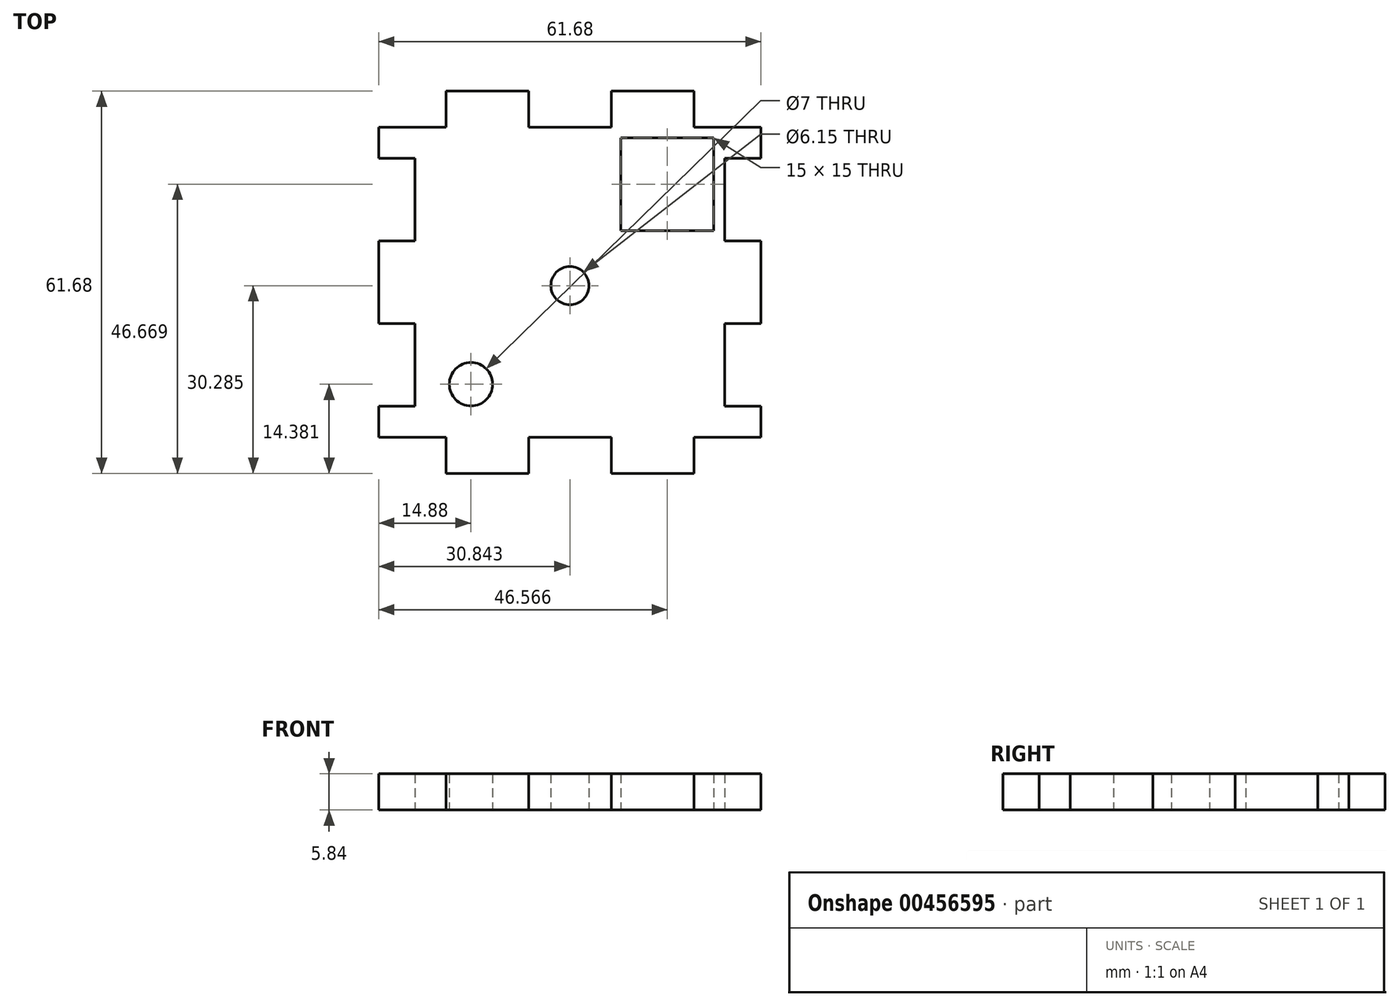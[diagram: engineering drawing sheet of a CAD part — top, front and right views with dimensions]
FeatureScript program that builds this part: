
annotation { "Feature Type Name" : "Feature", "Feature Type Description" : "" }
export const myFeature = defineFeature(function(context is Context, id is Id, definition is map)
    precondition{}
    {
        {
            var Q0;
            Q0=qCreatedBy(makeId("Top.planeOp"),FACE);
            var sketch = newSketch(context, id + "F0", { "sketchPlane" : qUnion([Q0])});
            skLineSegment(sketch, "E0.bottom", {"start": v(-25, 25.5) * mm, "end": v(-20, 25.5) * mm});
            skLineSegment(sketch, "E0.top", {"start": v(-25, -24.5) * mm, "end": v(-20, -24.5) * mm});
            skLineSegment(sketch, "E0.left", {"start": v(-25, 20.5) * mm, "end": v(-25, 7.17) * mm});
            skLineSegment(sketch, "E0.right", {"start": v(25, 20.5) * mm, "end": v(25, 7.17) * mm});
            skLineSegment(sketch, "E1.bottom", {"start": v(-20, 31.35) * mm, "end": v(-6.67, 31.35) * mm});
            skLineSegment(sketch, "E1.top", {"start": v(-20, -30.33) * mm, "end": v(-6.67, -30.33) * mm});
            skLineSegment(sketch, "E1.left", {"start": v(-30.84, 25.5) * mm, "end": v(-30.84, 20.5) * mm});
            skLineSegment(sketch, "E1.right", {"start": v(30.84, 25.5) * mm, "end": v(30.84, 20.5) * mm});
            skCircle(sketch, "E2", {"center": v(-15.96, -15.95) * mm, "radius": 3.5 * mm});
            skLineSegment(sketch, "E3.bottom", {"start": v(8.23, 23.84) * mm, "end": v(23.23, 23.84) * mm});
            skLineSegment(sketch, "E3.top", {"start": v(8.23, 8.84) * mm, "end": v(23.23, 8.84) * mm});
            skLineSegment(sketch, "E3.left", {"start": v(8.23, 23.84) * mm, "end": v(8.23, 8.84) * mm});
            skLineSegment(sketch, "E3.right", {"start": v(23.23, 23.84) * mm, "end": v(23.23, 8.84) * mm});
            skLineSegment(sketch, "E4", {"start": v(8.23, 16.34) * mm, "end": v(23.23, 16.34) * mm, "construction": true});
            skLineSegment(sketch, "E5.top", {"start": v(20, 25.5) * mm, "end": v(30.84, 25.5) * mm});
            skLineSegment(sketch, "E5.left", {"start": v(20, 31.35) * mm, "end": v(20, 25.5) * mm});
            skLineSegment(sketch, "E6.top", {"start": v(30.84, -24.5) * mm, "end": v(20, -24.5) * mm});
            skLineSegment(sketch, "E6.right", {"start": v(20, -30.33) * mm, "end": v(20, -24.5) * mm});
            skLineSegment(sketch, "E7.top", {"start": v(-30.84, -24.5) * mm, "end": v(-20, -24.5) * mm});
            skLineSegment(sketch, "E7.right", {"start": v(-20, -30.33) * mm, "end": v(-20, -24.5) * mm});
            skLineSegment(sketch, "E8.bottom", {"start": v(-6.67, -24.5) * mm, "end": v(6.67, -24.5) * mm});
            skLineSegment(sketch, "E8.left", {"start": v(-6.67, -24.5) * mm, "end": v(-6.67, -30.33) * mm});
            skLineSegment(sketch, "E8.right", {"start": v(6.67, -24.5) * mm, "end": v(6.67, -30.33) * mm});
            skLineSegment(sketch, "E9.bottom", {"start": v(-30.84, 20.5) * mm, "end": v(-25, 20.5) * mm});
            skLineSegment(sketch, "E9.top", {"start": v(-30.84, 7.17) * mm, "end": v(-25, 7.17) * mm});
            skLineSegment(sketch, "E10.bottom", {"start": v(-30.84, -6.16) * mm, "end": v(-25, -6.16) * mm});
            skLineSegment(sketch, "E10.top", {"start": v(-30.84, -19.5) * mm, "end": v(-25, -19.5) * mm});
            skLineSegment(sketch, "E10.right", {"start": v(-25, -6.16) * mm, "end": v(-25, -19.5) * mm});
            skLineSegment(sketch, "E11.top", {"start": v(-30.84, 25.5) * mm, "end": v(-20, 25.5) * mm});
            skLineSegment(sketch, "E11.right", {"start": v(-20, 31.35) * mm, "end": v(-20, 25.5) * mm});
            skLineSegment(sketch, "E12.top", {"start": v(-6.67, 25.5) * mm, "end": v(6.67, 25.5) * mm});
            skLineSegment(sketch, "E12.left", {"start": v(-6.67, 31.35) * mm, "end": v(-6.67, 25.5) * mm});
            skLineSegment(sketch, "E12.right", {"start": v(6.67, 31.35) * mm, "end": v(6.67, 25.5) * mm});
            skLineSegment(sketch, "E13.bottom", {"start": v(25, 20.5) * mm, "end": v(30.84, 20.5) * mm});
            skLineSegment(sketch, "E13.top", {"start": v(25, 7.17) * mm, "end": v(30.84, 7.17) * mm});
            skLineSegment(sketch, "E14.bottom", {"start": v(25, -6.16) * mm, "end": v(30.84, -6.16) * mm});
            skLineSegment(sketch, "E14.top", {"start": v(25, -19.5) * mm, "end": v(30.84, -19.5) * mm});
            skLineSegment(sketch, "E14.left", {"start": v(25, -6.16) * mm, "end": v(25, -19.5) * mm});
            skLineSegment(sketch, "E15.trimOffspring", {"start": v(6.67, 31.35) * mm, "end": v(20, 31.35) * mm});
            skLineSegment(sketch, "E16.trimOffspring", {"start": v(30.84, 7.17) * mm, "end": v(30.84, -6.16) * mm});
            skLineSegment(sketch, "E17.trimOffspring", {"start": v(30.84, -19.5) * mm, "end": v(30.84, -24.5) * mm});
            skLineSegment(sketch, "E18.trimOffspring", {"start": v(20, -24.5) * mm, "end": v(25, -24.5) * mm});
            skLineSegment(sketch, "E19.trimOffspring", {"start": v(6.67, -30.33) * mm, "end": v(20, -30.33) * mm});
            skLineSegment(sketch, "E20.trimOffspring", {"start": v(-30.84, -19.5) * mm, "end": v(-30.84, -24.5) * mm});
            skLineSegment(sketch, "E21.trimOffspring", {"start": v(-30.84, 7.17) * mm, "end": v(-30.84, -6.16) * mm});
            skLineSegment(sketch, "E22.trimOffspring", {"start": v(20, 25.5) * mm, "end": v(25, 25.5) * mm});
            skCircle(sketch, "E23", {"center": v(0, -0.04) * mm, "radius": 3.08 * mm});
            skSolve(sketch);
        }
        {
            var Q0;
            Q0=makeQuery(id+"F0.imprint","IMPRINT",FACE,{"disambiguationData":[TD([[makeQuery(id+"F0.imprint","IMPRINT",EDGE,{"derivedFrom":sQuery(id+"F0.wireOp",EDGE,"E1.bottom")}),-1.0]])]});
            extrude(context, id + "F1", {"entities" : qUnion([Q0]), "depth" : 5.84 * mm});
        }
    });
